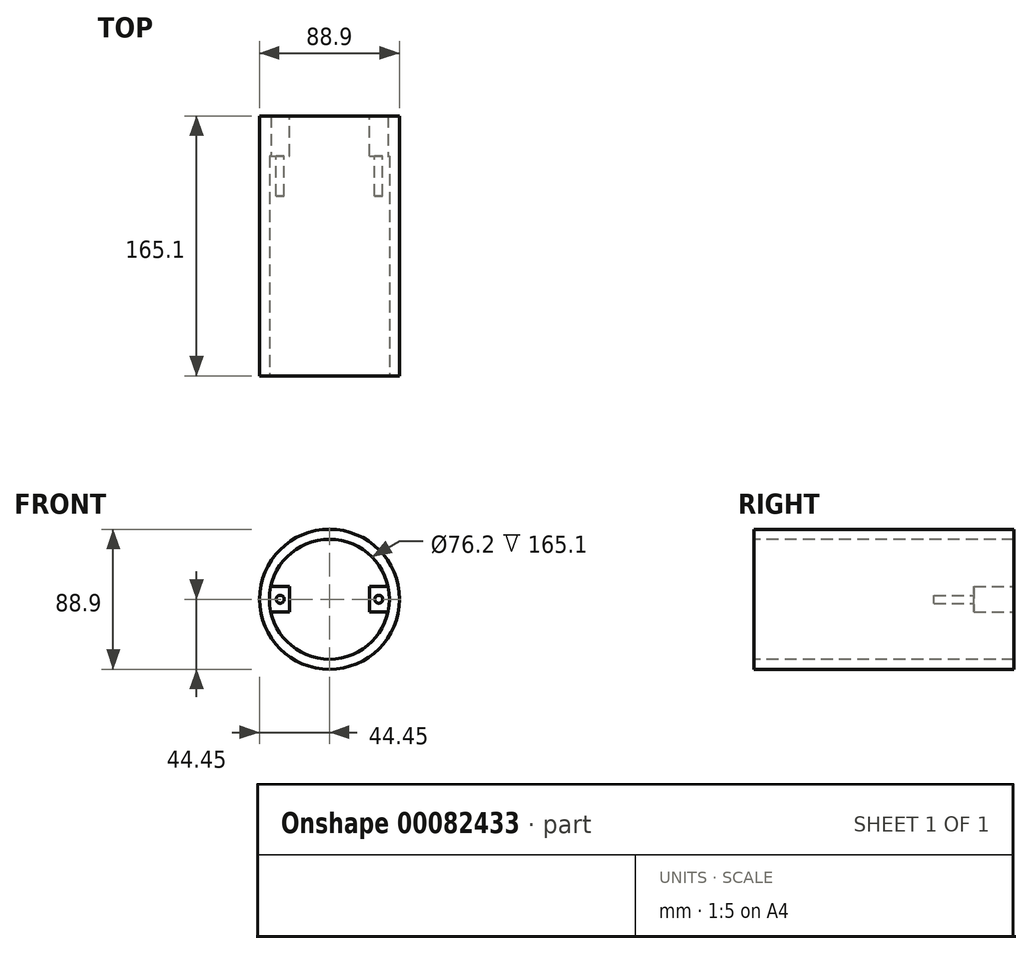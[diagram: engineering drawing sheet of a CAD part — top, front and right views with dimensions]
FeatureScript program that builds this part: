
annotation { "Feature Type Name" : "Feature", "Feature Type Description" : "" }
export const myFeature = defineFeature(function(context is Context, id is Id, definition is map)
    precondition{}
    {
        {
            var Q0;
            Q0=qCreatedBy(makeId("Front.planeOp"),FACE);
            var sketch = newSketch(context, id + "F0", { "sketchPlane" : qUnion([Q0])});
            skCircle(sketch, "E0", {"center": v(0, 0) * mm, "radius": 44.45 * mm});
            skSolve(sketch);
        }
        {
            var Q0;
            Q0 = qSketchRegion(id + "F0", true);
            extrude(context, id + "F1", {"entities" : qUnion([Q0]), "depth" : 165.1 * mm});
        }
        {
            var Q0;
            Q0=makeQuery(id+"F1.opExtrude","CAP_FACE",FACE,{"disambiguationData":[OSD([sQuery(id+"F0.wireOp",EDGE,"E0")])],"isStart":false});
            var sketch = newSketch(context, id + "F2", { "sketchPlane" : qUnion([Q0])});
            skCircle(sketch, "E1", {"center": v(0, 0) * mm, "radius": 38.1 * mm});
            skSolve(sketch);
        }
        {
            var Q0;
            Q0=makeQuery(id+"F2.imprint","IMPRINT",FACE,{"disambiguationData":[TD([[makeQuery(id+"F2.imprint","IMPRINT",EDGE,{"derivedFrom":sQuery(id+"F2.wireOp",EDGE,"E1")}),1.0]])]});
            extrude(context, id + "F3", {"entities" : qUnion([Q0]), "operationType" : NewBodyOperationType.REMOVE, "oppositeDirection" : true, "depth" : 254 * mm});
        }
        {
            var Q0;
            Q0=qCreatedBy(makeId("Front.planeOp"),FACE);
            var sketch = newSketch(context, id + "F4", { "sketchPlane" : qUnion([Q0])});
            skLineSegment(sketch, "E2.bottom", {"start": v(-43.36, 8.13) * mm, "end": v(43.36, 8.13) * mm});
            skLineSegment(sketch, "E2.top", {"start": v(-43.36, -8.13) * mm, "end": v(43.36, -8.13) * mm});
            skLineSegment(sketch, "E2.left", {"start": v(-43.36, 8.13) * mm, "end": v(-43.36, -8.13) * mm});
            skLineSegment(sketch, "E2.right", {"start": v(43.36, 8.13) * mm, "end": v(43.36, -8.13) * mm});
            skPoint(sketch, "E2.middle", {"position": v(0, 0) * mm});
            skSolve(sketch);
        }
        {
            var Q0;
            Q0 = qSketchRegion(id + "F4", true);
            extrude(context, id + "F5", {"entities" : qUnion([Q0]), "operationType" : NewBodyOperationType.ADD, "depth" : 25.4 * mm});
        }
        {
            var Q0;
            Q0=makeQuery(id+"F5.boolean.opBoolean","MERGE",FACE,{"derivedFrom":[makeQuery(id+"F1.opExtrude","CAP_FACE",FACE,{"disambiguationData":[OSD([sQuery(id+"F0.wireOp",EDGE,"E0")])],"isStart":true}),makeQuery(id+"F5.opExtrude","CAP_FACE",FACE,{"disambiguationData":[OSD([sQuery(id+"F4.wireOp",EDGE,"E2.bottom"),sQuery(id+"F4.wireOp",EDGE,"E2.top"),sQuery(id+"F4.wireOp",EDGE,"E2.left"),sQuery(id+"F4.wireOp",EDGE,"E2.right")])],"isStart":true})]});
            var sketch = newSketch(context, id + "F6", { "sketchPlane" : qUnion([Q0])});
            skPoint(sketch, "E3.middle", {"position": v(0, 0) * mm});
            skLineSegment(sketch, "E4.bottom", {"start": v(25.4, -8.13) * mm, "end": v(-25.4, -8.13) * mm});
            skLineSegment(sketch, "E4.top", {"start": v(25.4, 8.13) * mm, "end": v(-25.4, 8.13) * mm});
            skLineSegment(sketch, "E4.left", {"start": v(25.4, -8.13) * mm, "end": v(25.4, 8.13) * mm});
            skLineSegment(sketch, "E4.right", {"start": v(-25.4, -8.13) * mm, "end": v(-25.4, 8.13) * mm});
            skSolve(sketch);
        }
        {
            var Q0;
            Q0 = qSketchRegion(id + "F6", true);
            extrude(context, id + "F7", {"entities" : qUnion([Q0]), "operationType" : NewBodyOperationType.REMOVE, "oppositeDirection" : true, "depth" : 25.4 * mm});
        }
        {
            var Q0;
            {var subQ0=sQuery(id+"F4.wireOp",EDGE,"E2.bottom");var subQ1=sQuery(id+"F4.wireOp",EDGE,"E2.top");Q0=makeQuery(id+"F7.boolean.opBoolean","SPLIT",FACE,{"disambiguationData":[TD([makeQuery(id+"F7.opExtrude","SWEPT_FACE",FACE,{"disambiguationData":[OSD([sQuery(id+"F6.wireOp",EDGE,"E4.right")])]})])],"derivedFrom":makeQuery(id+"F5.opExtrude","CAP_FACE",FACE,{"disambiguationData":[OSD([subQ0,subQ1,sQuery(id+"F4.wireOp",EDGE,"E2.left"),sQuery(id+"F4.wireOp",EDGE,"E2.right")])],"isStart":false})});}
            var sketch = newSketch(context, id + "F8", { "sketchPlane" : qUnion([Q0])});
            skCircle(sketch, "E5", {"center": v(31.31, 0) * mm, "radius": 2.54 * mm});
            skPoint(sketch, "E5.centerSnap0", {"position": v(31.31, 8.13) * mm});
            skPoint(sketch, "E5.centerSnap1", {"position": v(25.4, 0) * mm});
            skLineSegment(sketch, "E6", {"start": v(0, 44.98) * mm, "end": v(0, -48) * mm, "construction": true});
            skCircle(sketch, "E7.MirrorC", {"center": v(-31.31, 0) * mm, "radius": 2.54 * mm});
            skSolve(sketch);
        }
        {
            var Q0;
            Q0 = qSketchRegion(id + "F8", true);
            extrude(context, id + "F9", {"entities" : qUnion([Q0]), "operationType" : NewBodyOperationType.ADD, "depth" : 25.4 * mm});
        }
    });
